# Revit family: Furniture-Floor_Mount-Vanity-KOHLER-Hadron-K-39607-1
name_source: partatom
category: Plumbing Fixtures
units: mm (PartAtom-declared; Revit-internal decimal feet)

## family parameters
Cut with Voids When Loaded = No
Host = Face
Maintain Annotation Orientation = No
OmniClass Number = 23.31.13.00
Part Type = Normal
Room Calculation Point = No
Round Connector Dimension = Use Diameter
Shared = No

## types (3) — shared parameters
ADA Compliant = No
Assembly Code = D2010400
CW Connection = No
Cold Water Inlet = Cold Water Inlet
Date Modified = 06/05/2025
Description = 60 Inch bathroom vanity cabinet with sinks and quartz top
Drain Included = No
HW Connection = No
Hardware Included = Yes
Height = 1010.6 mm
Hot Water Inlet = Hot Water Inlet
Length = 539.254 mm
Manufacturer = Kohler Co.
Master Format 2014 = 22 41 16
Master Format 2014 Name = Residential Lavatories and Sinks
Material = Solid Wood Construction
Product Documentation Link = https://www.us.kohler.com
Product Name = Hadron
Product Page URL = http://www.us.kohler.com
URL = https://www.us.kohler.com
Vent Connection = No
Waste Connection = Yes
Waste Water Outlet 1 = Waste Water Outlet 1
Waste Water Outlet 2 = Waste Water Outlet 2
WaterSense Certified = No
Width = 1542.951 mm
zero-valued in all types: Default Elevation

## per-type parameters (varying)
| type | Finish | Model | Secondary Finish | Type |
| 0-White | Kohler-Wood-Molded-0-White | K-39607-ASB-0 | Kohler-Wood-Molded-0-White | 1 |
| AGA-Ash Grey | KOHLER-Wood-AGA-Ash_Grey | K-39607-ASB-AGA | KOHLER-Wood-AGA-Ash_Grey | 2 |
| WEK-Weathered Oak | KOHLER-Wood-WEK-Weathered_Oak | K-39607-ASB-WEK | Kohler-Wood-Molded-0-White | 3 |

## geometry (parser evidence)
native form markers: Sweep x5
no freeform markers — native parametric forms only
